# Revit family: NLRS_57_AIR_UN_duct-diffuser-wuck-supply_LT_sacs
name_source: partatom
category: Air Terminals
units: mm (PartAtom-declared; Revit-internal decimal feet)

## family parameters
Always vertical = Yes
Cut with Voids When Loaded = No
Part Type = Normal
Room Calculation Point = No
Round Connector Dimension = Use Diameter
Shared = No
Work Plane-Based = No

## types (16) — shared parameters
Assembly Code = 57
Description = Grill for round duct, type WUCK (supply)
FireRating = 00
IfcDescription = Grill for round duct, type WUCK (supply)
IfcExportAs = IfcAirterminal
IfcExportType = Diffuser
IsExternal = No
LoadBearing = No
Model = WUCK
NLRS_C_content_datum_uitgifte = 13-04-2023
NLRS_C_content_provider = Solid Air Climate Solutions
NLRS_C_content_versie = 3.20.01
SACS_Article_Data = WUCK_Data
URL = https://solid-air.nl
zero-valued in all types: Default Elevation

## per-type parameters (varying)
| type | Max Flow | Min Flow | SACS_Factor_LpF1 | SACS_Factor_LpF2 | SACS_Factor_PsF1 | SACS_Factor_PsF2 | SACS_Factor_WF1 | SACS_Factor_WF2 | SACS_Price_Height | SACS_Price_Width | SACS_Product_Cost |
| 215x65 | 144.0 m³/h | 72.0 m³/h | -20.315454 | 8.479393 | 587.901846 | 1.775568 | 0.034484 | 0.971571 | 65 mm  [stored 0.213255 ft] | 215 mm | 26 $ |
| 315x65 | 216.0 m³/h | 90.0 m³/h | -15.053517 | 7.090116 | 313.033159 | 1.762374 | 0.023407 | 1.012545 | 65 mm  [stored 0.213255 ft] | 315 mm  [stored 1.03346 ft] | 29 $ |
| 415x65 | 288.0 m³/h | 144.0 m³/h | -24.454357 | 8.764233 | 170.684596 | 1.78026 | 0.02046 | 1.009019 | 65 mm  [stored 0.213255 ft] | 415 mm  [stored 1.36155 ft] | 34 $ |
| 515x65 | 360.0 m³/h | 144.0 m³/h | -20.042638 | 7.795303 | 156.576398 | 1.72695 | 0.019444 | 1 | 65 mm  [stored 0.213255 ft] | 515 mm  [stored 1.68963 ft] | 37 $ |
| 615x65 | 450.0 m³/h | 180.0 m³/h | -20.529538 | 7.737214 | 79.982181 | 1.790013 | 0.017369 | 1.003838 | 65 mm  [stored 0.213255 ft] | 615 mm  [stored 2.01772 ft] | 41 $ |
| 815x65 | 450.0 m³/h | 252.0 m³/h | -18.107367 | 7.091224 | 26.904344 | 1.878606 | 0.089829 | 0.693942 | 65 mm  [stored 0.213255 ft] | 815 mm  [stored 2.67388 ft] | 49 $ |
| 215x115 | 288.0 m³/h | 144.0 m³/h | -24.134005 | 8.6669 | 233.027072 | 1.726149 | 0.022222 | 1 | 115 mm  [stored 0.377297 ft] | 215 mm | 30 $ |
| 315x115 | 360.0 m³/h | 180.0 m³/h | -17.614518 | 7.200584 | 130.747087 | 1.704401 | 0.018855 | 0.995281 | 115 mm  [stored 0.377297 ft] | 315 mm  [stored 1.03346 ft] | 0 $ |
| 415x115 | 540.0 m³/h | 216.0 m³/h | -22.967279 | 7.970362 | 82.613363 | 1.70168 | 0.015194 | 1.007765 | 115 mm  [stored 0.377297 ft] | 415 mm  [stored 1.36155 ft] | 42 $ |
| 515x115 | 720.0 m³/h | 288.0 m³/h | -23.753629 | 8.017527 | 47.221865 | 1.73121 | 0.013415 | 1.009709 | 115 mm  [stored 0.377297 ft] | 515 mm  [stored 1.68963 ft] | 47 $ |
| 615x115 | 720.0 m³/h | 360.0 m³/h | -21.305642 | 7.488992 | 44.618746 | 1.688575 | 0.013472 | 0.995451 | 115 mm  [stored 0.377297 ft] | 615 mm  [stored 2.01772 ft] | 50 $ |
| 815x115 | 1080.0 m³/h | 450.0 m³/h | -24.360637 | 7.796812 | 18.11387 | 1.753749 | 0.010831 | 1.007249 | 115 mm  [stored 0.377297 ft] | 815 mm  [stored 2.67388 ft] | 60 $ |
| 415x215 | 1080.0 m³/h | 540.0 m³/h | -20.489694 | 7.225646 | 16.708639 | 1.762043 | 0.010713 | 1.011078 | 215 mm | 415 mm  [stored 1.36155 ft] | 54 $ |
| 515x215 | 1440.0 m³/h | 540.0 m³/h | -29.007795 | 8.40577 | 16.206682 | 1.713363 | 0.010778 | 0.994436 | 215 mm | 515 mm  [stored 1.68963 ft] | 60 $ |
| 615x215 | 1440.0 m³/h | 720.0 m³/h | -21.518736 | 7.225646 | 19.269996 | 1.643009 | 0.009444 | 1 | 215 mm | 615 mm  [stored 2.01772 ft] | 70 $ |
| 815x215 | 2160.0 m³/h | 1080.0 m³/h | -23.693844 | 7.399644 | 5.592749 | 1.747947 | 0.008547 | 0.994574 | 215 mm | 815 mm  [stored 2.67388 ft] | 0 $ |

note: [stored X ft] marks values corroborated as IEEE doubles in the binary element streams (Revit-internal decimal feet)

## geometry (parser evidence)
native form markers: Sweep x23
no freeform markers — native parametric forms only
